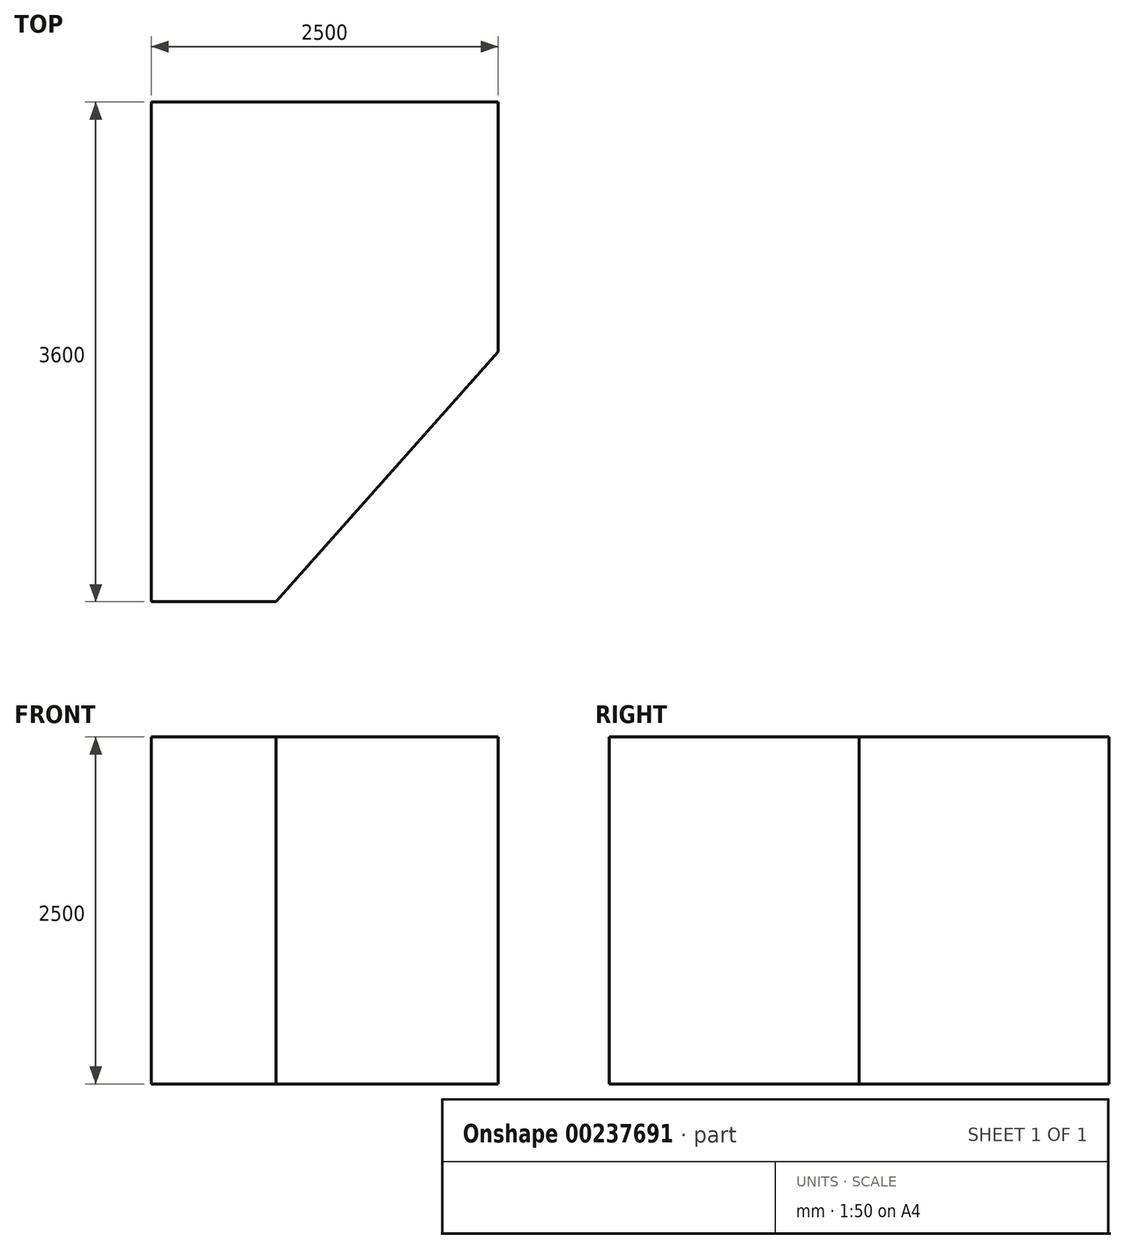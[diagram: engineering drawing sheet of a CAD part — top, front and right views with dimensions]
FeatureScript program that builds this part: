
annotation { "Feature Type Name" : "Feature", "Feature Type Description" : "" }
export const myFeature = defineFeature(function(context is Context, id is Id, definition is map)
    precondition{}
    {
        {
            var Q0;
            Q0=qCreatedBy(makeId("Top.planeOp"),FACE);
            var sketch = newSketch(context, id + "F0", { "sketchPlane" : qUnion([Q0])});
            skLineSegment(sketch, "E0.bottom", {"start": v(-350, -1800) * mm, "end": v(-1250, -1800) * mm});
            skLineSegment(sketch, "E0.top", {"start": v(1250, 1800) * mm, "end": v(-1250, 1800) * mm});
            skLineSegment(sketch, "E0.left", {"start": v(1250, 0) * mm, "end": v(1250, 1800) * mm});
            skLineSegment(sketch, "E0.right", {"start": v(-1250, -1800) * mm, "end": v(-1250, 1800) * mm});
            skPoint(sketch, "E0.middle", {"position": v(0, 0) * mm});
            skLineSegment(sketch, "E1", {"start": v(1250, 0) * mm, "end": v(-350, -1800) * mm});
            skPoint(sketch, "E2.orphan", {"position": v(1250, -1800) * mm});
            skSolve(sketch);
        }
        {
            var Q0;
            Q0 = qSketchRegion(id + "F0", true);
            extrude(context, id + "F1", {"entities" : qUnion([Q0]), "depth" : 2500 * mm});
        }
    });
